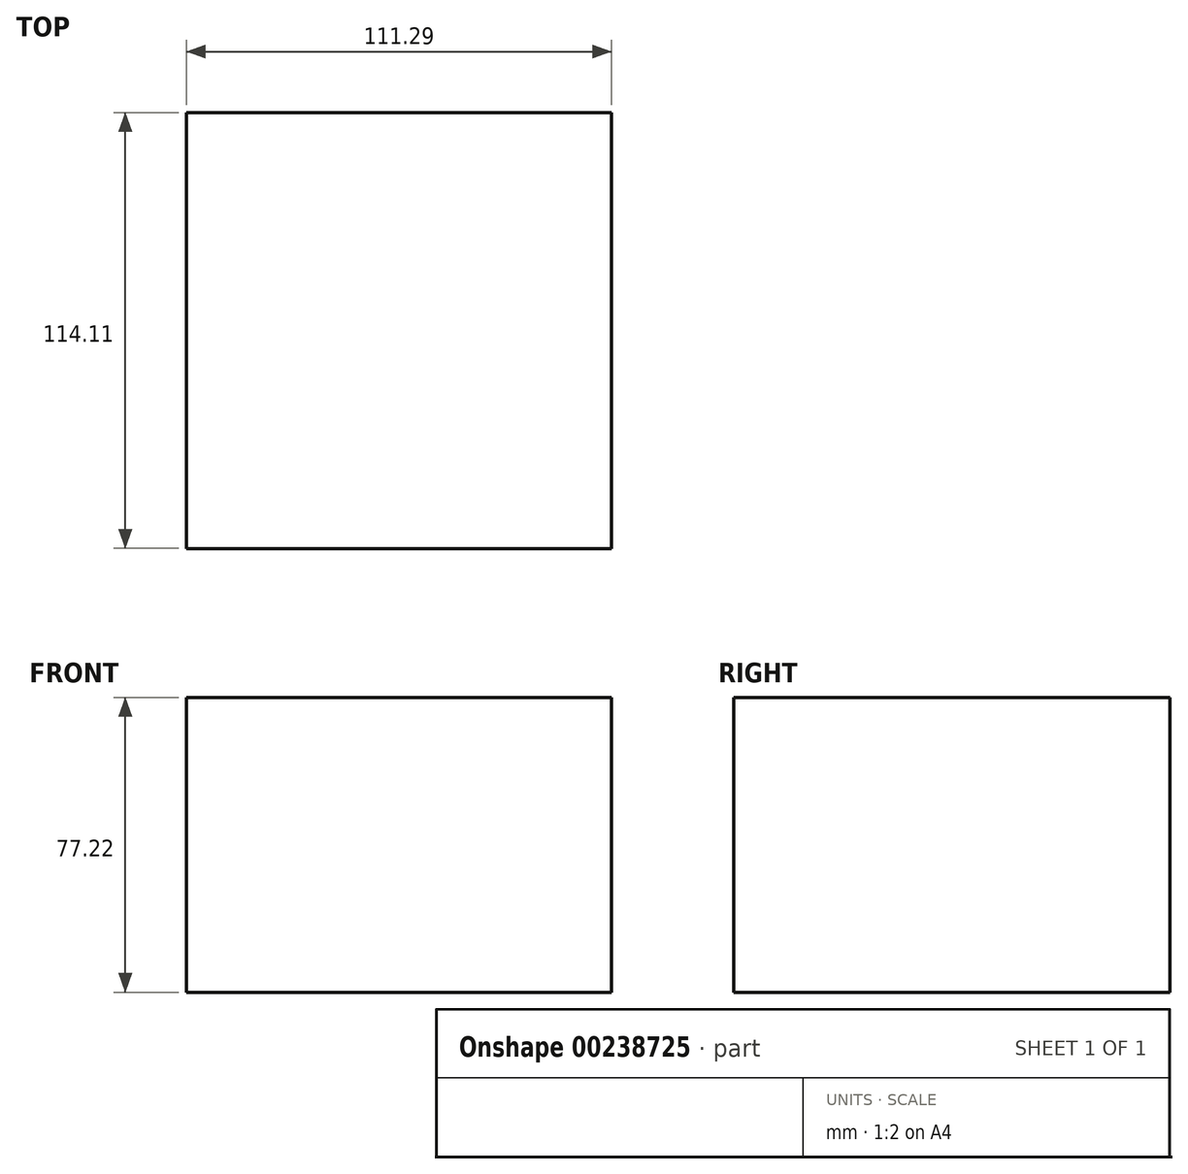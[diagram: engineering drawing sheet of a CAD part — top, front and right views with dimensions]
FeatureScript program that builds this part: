
annotation { "Feature Type Name" : "Feature", "Feature Type Description" : "" }
export const myFeature = defineFeature(function(context is Context, id is Id, definition is map)
    precondition{}
    {
        {
            var Q0;
            Q0=qCreatedBy(makeId("Top.planeOp"),FACE);
            var sketch = newSketch(context, id + "F0", { "sketchPlane" : qUnion([Q0])});
            skLineSegment(sketch, "E0.bottom", {"start": v(-84.38, 52.86) * mm, "end": v(26.9, 52.86) * mm});
            skLineSegment(sketch, "E0.top", {"start": v(-84.38, -61.25) * mm, "end": v(26.9, -61.25) * mm});
            skLineSegment(sketch, "E0.left", {"start": v(-84.38, 52.86) * mm, "end": v(-84.38, -61.25) * mm});
            skLineSegment(sketch, "E0.right", {"start": v(26.9, 52.86) * mm, "end": v(26.9, -61.25) * mm});
            skSolve(sketch);
        }
        {
            var Q0;
            Q0 = qSketchRegion(id + "F0", true);
            extrude(context, id + "F1", {"entities" : qUnion([Q0]), "depth" : 77.22 * mm});
        }
    });
